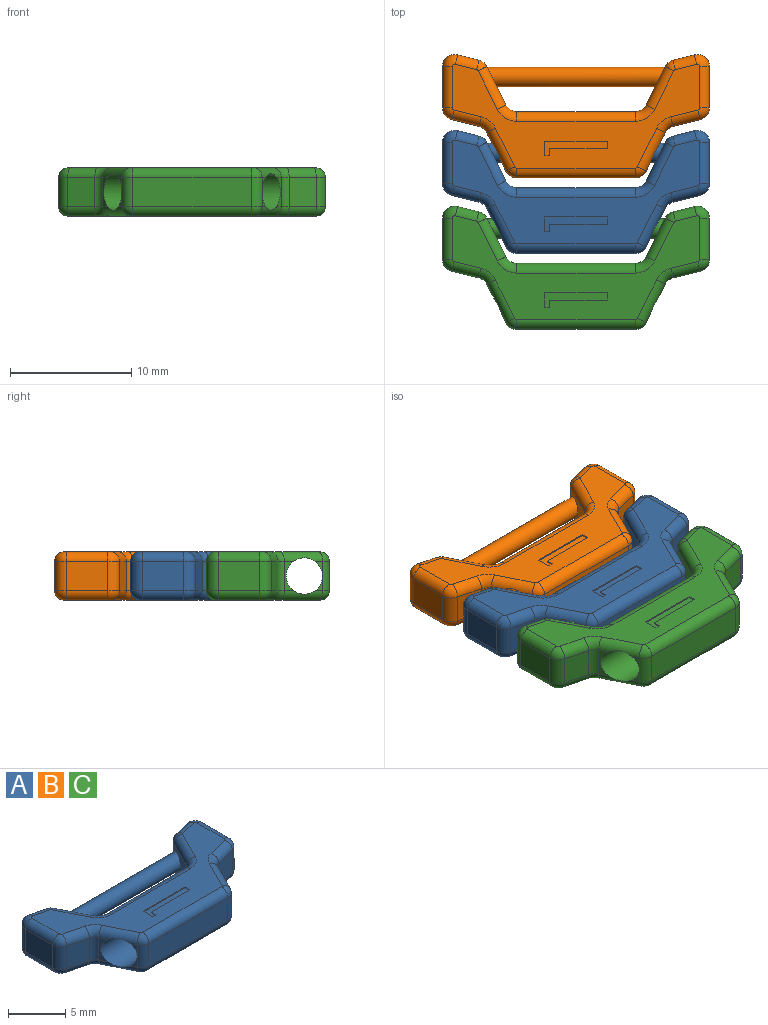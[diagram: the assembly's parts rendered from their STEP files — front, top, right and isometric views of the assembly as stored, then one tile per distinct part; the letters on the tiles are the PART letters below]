
ASSEMBLY  parts=3 mates=2
PART A: 85 faces, bbox 22.2x10.3x4.2 mm
  f0: plane 20.4x8.57mm, normal (0,0,1), area 67.3mm2, adj f28,f29,f30,f31,f32,f33,f34,f35
  f1: plane 2.4x0.61mm, normal (0.89,-0.45,0), area 0.5mm2, adj f16,f42,f65,f76
  f2: plane 2.4x0.76mm, normal (-0.89,-0.45,0), area 0.9mm2, adj f26,f50,f73,f76
  f3: plane 9.76x2.4mm, normal (0,-1,0), area 23.4mm2, adj f16,f27,f46,f69
  f4: plane 2.4x0.76mm, normal (0.89,-0.45,0), area 0.9mm2, adj f17,f42,f65,f76
  f5: plane 2.4x2.24mm, normal (0.24,-0.97,0), area 5.5mm2, adj f17,f18,f38,f61
  f6: plane 3.39x2.4mm, normal (1,0,0), area 8.1mm2, adj f18,f19,f34,f57
  f7: plane 2.4x1.75mm, normal (-0.24,0.97,0), area 4.3mm2, adj f19,f20,f30,f53
  f8: plane 3.34x2.57mm, normal (-0.89,0.45,0), area 6.3mm2, adj f20,f21,f29,f54,f77
  f9: plane 9.76x2.4mm, normal (0,1,0), area 23.4mm2, adj f21,f22,f33,f58
  f10: plane 3.17x2.4mm, normal (0.89,0.45,0), area 6.3mm2, adj f22,f23,f37,f62,f77
  f11: plane 2.4x1.75mm, normal (0.24,0.97,0), area 4.3mm2, adj f23,f24,f41,f66
  f12: plane 3.39x2.4mm, normal (-1,0,0), area 8.1mm2, adj f24,f25,f45,f70
  f13: plane 2.4x2.24mm, normal (-0.24,-0.97,0), area 5.5mm2, adj f25,f26,f49,f74
  f14: plane 2.4x0.61mm, normal (-0.89,-0.45,0), area 0.5mm2, adj f27,f50,f73,f76
  f15: plane 20.4x8.57mm, normal (0,0,-1), area 70.6mm2, adj f52,f53,f54,f55,f56,f57,f58,f59
  f16: cylinder r=1mm len=2.4mm, axis (0,0,1), area 2.7mm2, adj f1,f3,f44,f67
  f17: cylinder r=1mm len=2.4mm, axis (0,0,1), area 2.1mm2, adj f4,f5,f40,f63
  f18: cylinder r=1mm len=2.4mm, axis (0,0,-1), area 3.2mm2, adj f5,f6,f36,f59
  f19: cylinder r=1mm len=2.4mm, axis (0,0,-1), area 4.4mm2, adj f6,f7,f32,f55
  f20: cylinder r=1mm len=2.4mm, axis (0,0,-1), area 2.1mm2, adj f7,f8,f28,f52
  f21: cylinder r=1mm len=2.4mm, axis (0,0,1), area 2.7mm2, adj f8,f9,f31,f56
  f22: cylinder r=1mm len=2.4mm, axis (0,0,-1), area 2.7mm2, adj f9,f10,f35,f60
  f23: cylinder r=1mm len=2.4mm, axis (0,0,-1), area 2.1mm2, adj f10,f11,f39,f64
  f24: cylinder r=1mm len=2.4mm, axis (0,0,-1), area 4.4mm2, adj f11,f12,f43,f68
  f25: cylinder r=1mm len=2.4mm, axis (0,0,-1), area 3.2mm2, adj f12,f13,f47,f72
  f26: cylinder r=1mm len=2.4mm, axis (0,0,1), area 2.1mm2, adj f2,f13,f51,f75
  f27: cylinder r=1mm len=2.4mm, axis (0,0,-1), area 2.7mm2, adj f3,f14,f48,f71
  f28: torus R=0.2mm, axis (0,0,1), area 0.8mm2, adj f0,f20,f29,f30
  f29: cylinder r=0.8mm len=3.53mm, axis (0.45,0.89,0), area 4.5mm2, adj f0,f8,f28,f31
  f30: cylinder r=0.8mm len=1.94mm, axis (0.97,0.24,0), area 2.3mm2, adj f0,f7,f28,f32
  f31: torus R=1.8mm, axis (0,0,1), area 1.8mm2, adj f0,f21,f29,f33
  f32: torus R=0.2mm, axis (0,0,1), area 1.6mm2, adj f0,f19,f30,f34
  f33: cylinder r=0.8mm len=9.76mm, axis (1,0,0), area 12.3mm2, adj f0,f9,f31,f35
  f34: cylinder r=0.8mm len=3.39mm, axis (0,-1,0), area 4.3mm2, adj f0,f6,f32,f36
  f35: torus R=1.8mm, axis (0,0,1), area 1.8mm2, adj f0,f22,f33,f37
  f36: torus R=0.2mm, axis (0,0,1), area 1.2mm2, adj f0,f18,f34,f38
  f37: cylinder r=0.8mm len=3.53mm, axis (0.45,-0.89,0), area 4.5mm2, adj f0,f10,f35,f39
  f38: cylinder r=0.8mm len=2.43mm, axis (-0.97,-0.24,0), area 2.9mm2, adj f0,f5,f36,f40
  f39: torus R=0.2mm, axis (0,0,1), area 0.8mm2, adj f0,f23,f37,f41
  f40: torus R=1.8mm, axis (0,0,1), area 1.4mm2, adj f0,f17,f38,f42
  f41: cylinder r=0.8mm len=1.94mm, axis (0.97,-0.24,0), area 2.3mm2, adj f0,f11,f39,f43
  f42: cylinder r=0.8mm len=3.53mm, axis (-0.45,-0.89,0), area 4mm2, adj f0,f1,f4,f40,f44,f76
  f43: torus R=0.2mm, axis (0,0,1), area 1.6mm2, adj f0,f24,f41,f45
  f44: torus R=0.2mm, axis (0,0,1), area 1mm2, adj f0,f16,f42,f46
  f45: cylinder r=0.8mm len=3.39mm, axis (0,1,0), area 4.3mm2, adj f0,f12,f43,f47
  f46: cylinder r=0.8mm len=9.76mm, axis (-1,0,0), area 12.3mm2, adj f0,f3,f44,f48
  f47: torus R=0.2mm, axis (0,0,1), area 1.2mm2, adj f0,f25,f45,f49
  f48: torus R=0.2mm, axis (0,0,1), area 1mm2, adj f0,f27,f46,f50
  f49: cylinder r=0.8mm len=2.43mm, axis (-0.97,0.24,0), area 2.9mm2, adj f0,f13,f47,f51
  f50: cylinder r=0.8mm len=3.53mm, axis (-0.45,0.89,0), area 4mm2, adj f0,f2,f14,f48,f51,f76
  f51: torus R=1.8mm, axis (0,0,1), area 1.4mm2, adj f0,f26,f49,f50
  f52: torus R=0.2mm, axis (0,0,1), area 0.8mm2, adj f15,f20,f53,f54
  f53: cylinder r=0.8mm len=1.94mm, axis (-0.97,-0.24,0), area 2.3mm2, adj f7,f15,f52,f55
  f54: cylinder r=0.8mm len=3.53mm, axis (-0.45,-0.89,0), area 4.5mm2, adj f8,f15,f52,f56
  f55: torus R=0.2mm, axis (0,0,1), area 1.6mm2, adj f15,f19,f53,f57
  f56: torus R=1.8mm, axis (0,0,1), area 1.8mm2, adj f15,f21,f54,f58
  f57: cylinder r=0.8mm len=3.39mm, axis (0,1,0), area 4.3mm2, adj f6,f15,f55,f59
  f58: cylinder r=0.8mm len=9.76mm, axis (-1,0,0), area 12.3mm2, adj f9,f15,f56,f60
  f59: torus R=0.2mm, axis (0,0,1), area 1.2mm2, adj f15,f18,f57,f61
  f60: torus R=1.8mm, axis (0,0,1), area 1.8mm2, adj f15,f22,f58,f62
  f61: cylinder r=0.8mm len=2.43mm, axis (0.97,0.24,0), area 2.9mm2, adj f5,f15,f59,f63
  f62: cylinder r=0.8mm len=3.53mm, axis (-0.45,0.89,0), area 4.5mm2, adj f10,f15,f60,f64
  f63: torus R=1.8mm, axis (0,0,1), area 1.4mm2, adj f15,f17,f61,f65
  f64: torus R=0.2mm, axis (0,0,1), area 0.8mm2, adj f15,f23,f62,f66
  f65: cylinder r=0.8mm len=3.53mm, axis (0.45,0.89,0), area 4mm2, adj f1,f4,f15,f63,f67,f76
  f66: cylinder r=0.8mm len=1.94mm, axis (-0.97,0.24,0), area 2.3mm2, adj f11,f15,f64,f68
  f67: torus R=0.2mm, axis (0,0,1), area 1mm2, adj f15,f16,f65,f69
  f68: torus R=0.2mm, axis (0,0,1), area 1.6mm2, adj f15,f24,f66,f70
  f69: cylinder r=0.8mm len=9.76mm, axis (1,0,0), area 12.3mm2, adj f3,f15,f67,f71
  f70: cylinder r=0.8mm len=3.39mm, axis (0,-1,0), area 4.3mm2, adj f12,f15,f68,f72
  f71: torus R=0.2mm, axis (0,0,1), area 1mm2, adj f15,f27,f69,f73
  f72: torus R=0.2mm, axis (0,0,1), area 1.2mm2, adj f15,f25,f70,f74
  f73: cylinder r=0.8mm len=3.53mm, axis (0.45,-0.89,0), area 4mm2, adj f2,f14,f15,f71,f75,f76
  f74: cylinder r=0.8mm len=2.43mm, axis (0.97,-0.24,0), area 2.9mm2, adj f13,f15,f72,f75
  f75: torus R=1.8mm, axis (0,0,1), area 1.4mm2, adj f15,f26,f73,f74
  f76: cylinder r=1.5mm len=14.56mm, axis (1,0,0), area 123.1mm2, adj f1,f2,f4,f14,f42,f50,f65,f73
  f77: cylinder r=0.8mm len=14.66mm, axis (-1,0,0), area 69.7mm2, adj f8,f10
  f78: plane 0.6x0.1mm, normal (-1,0,0), area 0.1mm2, adj f0,f79,f83,f84
  f79: plane 5.15x0.1mm, normal (0,-1,0), area 0.5mm2, adj f0,f78,f80,f84
  f80: plane 1.2x0.1mm, normal (1,0,0), area 0.1mm2, adj f0,f79,f81,f84
  f81: plane 0.4x0.1mm, normal (0,1,0), area 0mm2, adj f0,f80,f82,f84
  f82: plane 0.6x0.1mm, normal (-1,0,0), area 0.1mm2, adj f0,f81,f83,f84
  f83: plane 4.75x0.1mm, normal (0,1,0), area 0.5mm2, adj f0,f78,f82,f84
  f84: plane 5.15x1.2mm, normal (0,0,1), area 3.3mm2, adj f78,f79,f80,f81,f82,f83
PART B: same geometry as A
PART C: same geometry as A
PLACE A t=(4.53,-9.07,-9.9)mm
PLACE B t=(4.53,-2.81,-9.9)mm
PLACE C t=(4.53,-15.32,-9.9)mm
MATE revolute B.f76 <-> A.f77  axis (1,0,0) through (4.53,-0.75,-9.9)mm
MATE revolute A.f76 <-> C.f77  axis (1,0,0) through (4.53,-7,-9.9)mm
